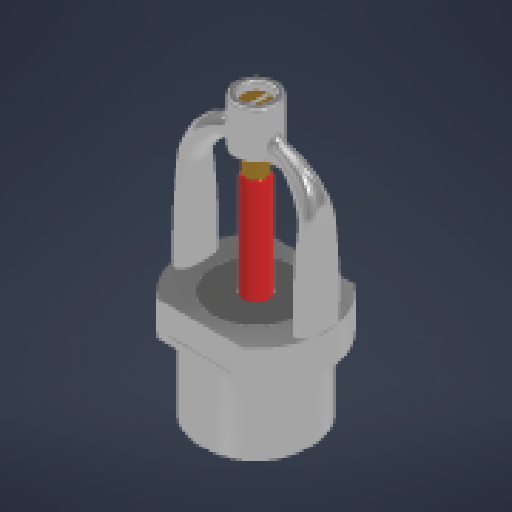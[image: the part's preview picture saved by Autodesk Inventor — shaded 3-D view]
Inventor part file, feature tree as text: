
AUTODESK INVENTOR PART (.ipt)
format: ipt  version: 2024 (Build 280153000, 153)  size: 1,179,648 bytes
history: native  units: mm
features: sketch x18, extrude x17, fillet x6, plane x2, other x2, emboss x1, chamfer x1, thread x1, projected_geometry x1
ambient origin geometry x8: Origin, YZ Plane, XZ Plane, XY Plane, X Axis, Y Axis, Z Axis, Center Point
bodies: Solid1 (feature_tree)
feature tree (49):
  plane  "Work Plane1"
  plane  "Work Plane2"
  extrude  "Extrusion2"  Depth=8.0mm
  fillet  "Fillet1"  Radius=1.5mm
  extrude  "Extrusion3"  Depth=8.0mm
  extrude  "Extrusion4"  Depth=26.0mm
  extrude  "Extrusion5"  Depth=4.0mm
  extrude  "Extrusion6"  Depth=27.0mm TaperAngle=0.0deg
  extrude  "Extrusion7"  Depth=27.0mm TaperAngle=0.0deg
  extrude  "Extrusion8"  Depth=27.0mm TaperAngle=0.0deg
  fillet  "Fillet2"  Radius=3.25mm
  fillet  "Fillet3"  Radius=0.2mm
  fillet  "Fillet4"  Radius=2.0mm
  fillet  "Fillet5"  Radius=2.0mm
  extrude  "Extrusion9"  Depth=10.5mm
  extrude  "Extrusion10"  Depth=16.0mm
  extrude  "Extrusion11"  Depth=5.0mm
  extrude  "Extrusion12"  Depth=4.9mm
  fillet  "Fillet7"  Radius=20.0mm
  extrude  "Extrusion13"  Depth=10.0mm TaperAngle=0.0deg
  extrude  "Extrusion14"  Depth=1.0mm TaperAngle=0.0deg
  extrude  "Extrusion15"  Depth=4.0mm
  emboss  "Emboss1"
  extrude  "Extrusion16"  Depth=0.2mm TaperAngle=0.0deg
  chamfer  "Chamfer1"  Distance=0.2mm
  extrude  "Extrusion17"  Depth=14.5mm TaperAngle=0.0deg
  extrude  "Extrusion18"  Depth=12.0mm
  thread  "Thread1"  [1 undecoded]
  other  "Edición directa1"
  sketch  "Sketch3"  dims[d5=4.0mm d14=-0.7mm d15=8.0mm d16=1.5mm d17=0.0mm]
  sketch  "Sketch4"  dims[d18=0.5mm d19=8.0mm]
  sketch  "Sketch5"  dims[d20=4.0mm d21=0.0mm d22=26.0mm]
  sketch  "Sketch6"  dims[d23=8.0mm d24=4.0mm]
  sketch  "Sketch7"  dims[d25=13.0mm d26=27.0mm d27=0.0mm]
  projected_geometry  "Projected Loop1"
  sketch  "Sketch8"  dims[d28=16.0mm d29=27.0mm d30=0.0mm]
  sketch  "Sketch9"  dims[d32=27.0mm d33=0.0mm d34=27.0mm d35=0.0mm d36=3.25mm d37=0.0mm d38=0.2mm d39=2.0mm d40=2.0mm]
  sketch  "Sketch10"  dims[d41=2.0mm d44=10.5mm]
  sketch  "Sketch11"  dims[d45=6.5mm d46=0.0mm d47=16.0mm]
  sketch  "Sketch12"  dims[d48=15.9mm d49=5.0mm]
  sketch  "Sketch13"  dims[d50=0.5mm d51=0.0mm d52=4.9mm d53=20.0mm d54=0.0mm]
  sketch  "Sketch14"  dims[d55=4.0mm d56=10.0mm d57=0.0mm]
  sketch  "Sketch15"  dims[d58=2.0mm d59=1.0mm d60=0.0mm]
  sketch  "Sketch16"  dims[d61=12.0mm d62=4.0mm]
  sketch  "Sketch17"  dims[d63=0.2mm d64=0.0mm d65=0.2mm d66=0.0mm d67=0.2mm d68=0.0mm]
  sketch  "Sketch18"  dims[d69=21.0mm d70=14.5mm d71=0.0mm]
  sketch  "Sketch19"  dims[d72=1.0mm d73=2.0mm d74=45.0deg d75=12.0mm d76=13.0mm d77=0.0mm]
  sketch  "Sketch20"  dims[d78=4.0mm d79=2.0mm d80=0.0mm d81=25.5mm d82=0.0mm d83=50.0mm d84=10.0mm d85=10.0mm]
  other  "Escala1"
note: 1 required parameter value undecoded (feature->parameter linkage not recoverable at this tier; creation-order binding heuristic only, values carry confidence <= 0.55)
